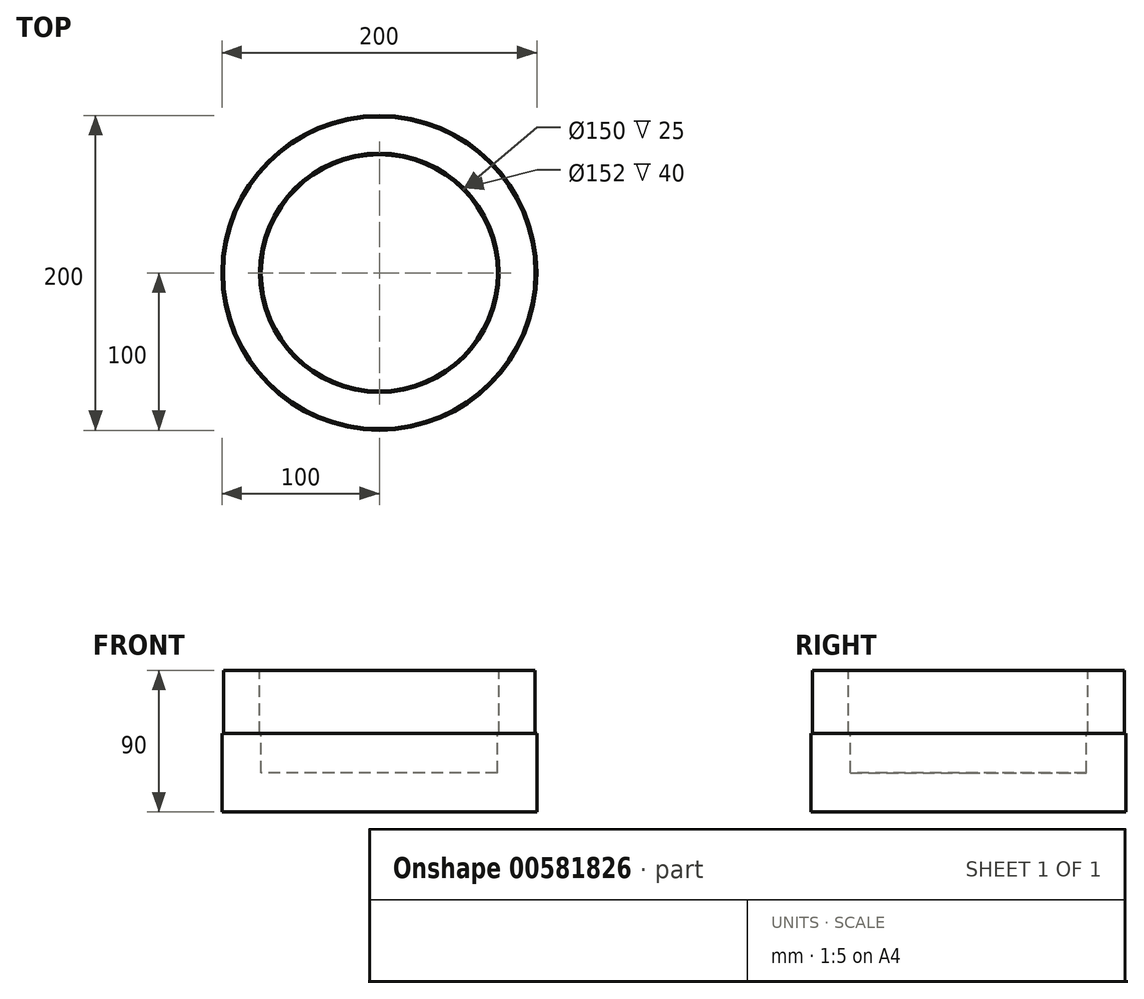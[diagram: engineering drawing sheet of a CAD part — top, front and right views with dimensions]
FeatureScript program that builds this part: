
annotation { "Feature Type Name" : "Feature", "Feature Type Description" : "" }
export const myFeature = defineFeature(function(context is Context, id is Id, definition is map)
    precondition{}
    {
        {
            var Q0;
            Q0=qCreatedBy(makeId("Front.planeOp"),FACE);
            var sketch = newSketch(context, id + "F0", { "sketchPlane" : qUnion([Q0])});
            skLineSegment(sketch, "E0", {"start": v(0, 136.7) * mm, "end": v(0, 0) * mm, "construction": true});
            skLineSegment(sketch, "E1", {"start": v(0, 0) * mm, "end": v(-100, 0) * mm});
            skLineSegment(sketch, "E2", {"start": v(-100, 0) * mm, "end": v(-100, 50) * mm});
            skLineSegment(sketch, "E3", {"start": v(-100, 50) * mm, "end": v(-99, 50) * mm});
            skLineSegment(sketch, "E4", {"start": v(-99, 50) * mm, "end": v(-99, 90) * mm});
            skLineSegment(sketch, "E5", {"start": v(-99, 90) * mm, "end": v(-76, 90) * mm});
            skLineSegment(sketch, "E6", {"start": v(-76, 90) * mm, "end": v(-76, 50) * mm});
            skLineSegment(sketch, "E7", {"start": v(-76, 50) * mm, "end": v(-75, 50) * mm});
            skLineSegment(sketch, "E8", {"start": v(-75, 50) * mm, "end": v(-75, 25) * mm});
            skLineSegment(sketch, "E9", {"start": v(-75, 25) * mm, "end": v(0, 25) * mm});
            skLineSegment(sketch, "E10", {"start": v(0, 25) * mm, "end": v(0, 0) * mm});
            skSolve(sketch);
        }
        {
            var Q0;
            Q0 = qSketchRegion(id + "F0", true);
            var Q1;
            Q1=sQuery(id+"F0.wireOp",EDGE,"E0");
            revolve(context, id + "F1", {"surfaceOperationType" : NewSurfaceOperationType.NEW, "entities" : qUnion([Q0]), "axis" : qUnion([Q1]), "revolveType" : RevolveType.FULL});
        }
    });
